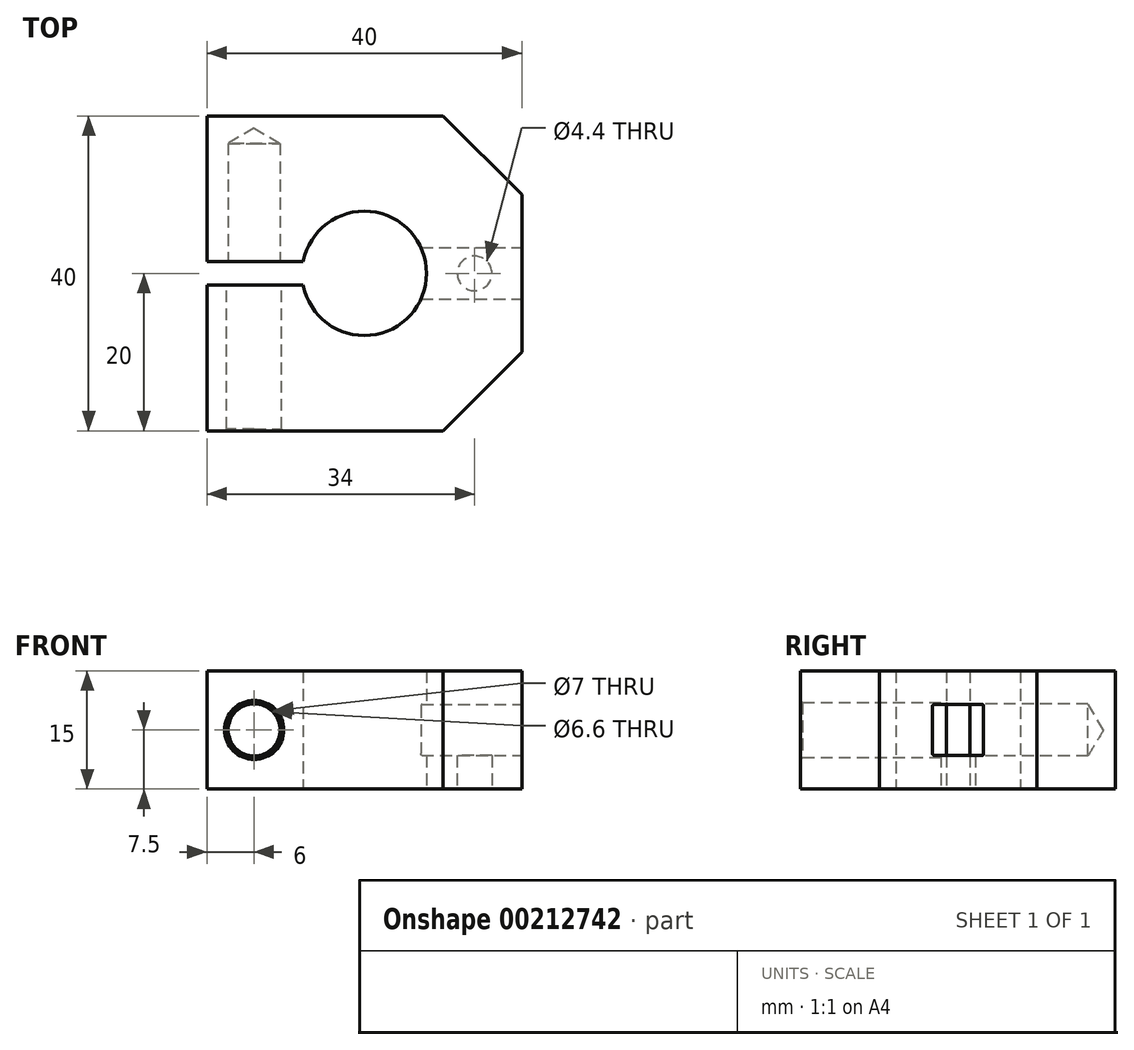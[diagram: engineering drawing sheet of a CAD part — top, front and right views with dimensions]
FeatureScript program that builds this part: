
annotation { "Feature Type Name" : "Feature", "Feature Type Description" : "" }
export const myFeature = defineFeature(function(context is Context, id is Id, definition is map)
    precondition{}
    {
        {
            var Q0;
            Q0=qCreatedBy(makeId("Top.planeOp"),FACE);
            var sketch = newSketch(context, id + "F0", { "sketchPlane" : qUnion([Q0])});
            skLineSegment(sketch, "E0.bottom", {"start": v(20, 20) * mm, "end": v(-20, 20) * mm});
            skLineSegment(sketch, "E0.top", {"start": v(20, -20) * mm, "end": v(-20, -20) * mm});
            skLineSegment(sketch, "E0.left", {"start": v(20, 20) * mm, "end": v(20, -20) * mm});
            skLineSegment(sketch, "E0.right", {"start": v(-20, 20) * mm, "end": v(-20, 1.5) * mm});
            skPoint(sketch, "E0.middle", {"position": v(0, 0) * mm});
            skArc(sketch, "E1", {"start": v(-7.76, -1.5) * mm, "mid": v(7.9, 0) * mm, "end": v(-7.76, 1.5) * mm});
            skLineSegment(sketch, "E2", {"start": v(-20, 0) * mm, "end": v(-7.9, 0) * mm, "construction": true});
            skLineSegment(sketch, "E3.0", {"start": v(-20, -1.5) * mm, "end": v(-7.76, -1.5) * mm});
            skLineSegment(sketch, "E4.0", {"start": v(-20, 1.5) * mm, "end": v(-7.76, 1.5) * mm});
            skLineSegment(sketch, "E5.trimOffspring", {"start": v(-20, -1.5) * mm, "end": v(-20, -20) * mm});
            skSolve(sketch);
        }
        {
            var Q0;
            Q0=makeQuery(id+"F0.imprint","IMPRINT",FACE,{"disambiguationData":[TD([[makeQuery(id+"F0.imprint","IMPRINT",EDGE,{"derivedFrom":sQuery(id+"F0.wireOp",EDGE,"E0.bottom")}),1.0]])]});
            extrude(context, id + "F1", {"entities" : qUnion([Q0]), "depth" : 15 * mm});
        }
        {
            var Q0;
            Q0=qCreatedBy(makeId("Front.planeOp"),FACE);
            var sketch = newSketch(context, id + "F2", { "sketchPlane" : qUnion([Q0])});
            skCircle(sketch, "E6", {"center": v(-14, 7.5) * mm, "radius": 3.5 * mm});
            skSolve(sketch);
        }
        {
            var Q0;
            Q0=makeQuery(id+"F2.imprint","IMPRINT",FACE,{"disambiguationData":[TD([[makeQuery(id+"F2.imprint","IMPRINT",EDGE,{"derivedFrom":sQuery(id+"F2.wireOp",EDGE,"E6")}),1.0]])]});
            extrude(context, id + "F3", {"entities" : qUnion([Q0]), "operationType" : NewBodyOperationType.REMOVE, "depth" : 25 * mm});
        }
        {
            var Q0;
            Q0=makeQuery(id+"F1.opExtrude","SWEPT_FACE",FACE,{"disambiguationData":[OSD([sQuery(id+"F0.wireOp",EDGE,"E4.0")])]});
            var sketch = newSketch(context, id + "F4", { "sketchPlane" : qUnion([Q0])});
            skPoint(sketch, "E7", {"position": v(-14, 7.5) * mm});
            skSolve(sketch);
        }
        {
            var Q0;
            Q0=sQuery(id+"F4.wireOp",VERTEX,"E7");
            var Q1;
            Q1=makeQuery(id+"F1.opExtrude","SWEPT_BODY",BODY,{"disambiguationData":[OSD([sQuery(id+"F0.wireOp",EDGE,"E0.bottom"),sQuery(id+"F0.wireOp",EDGE,"E0.top"),sQuery(id+"F0.wireOp",EDGE,"E0.left"),sQuery(id+"F0.wireOp",EDGE,"E0.right"),sQuery(id+"F0.wireOp",EDGE,"E1"),sQuery(id+"F0.wireOp",EDGE,"E3.0"),sQuery(id+"F0.wireOp",EDGE,"E4.0"),sQuery(id+"F0.wireOp",EDGE,"E5.trimOffspring")])]});
            hole(context, id + "F5", {"style" : HoleStyle.SIMPLE, "endStyle" : HoleEndStyle.BLIND, "standardTappedOrClearance" : lookupTablePath({ "standard" : "ISO", "fit" : "Normal", "size" : "M6", "type" : "Clearance" }), "standardBlindInLast" : lookupTablePath({ "fit" : "Standard", "standard" : "ISO", "size" : "M6", "type" : "Clearance" }), "holeDiameter" : 6.6 * mm, "holeDepth" : 15 * mm, "locations" : qUnion([Q0]), "scope" : qUnion([Q1])});
        }
        {
            var Q0;
            Q0=makeQuery(id+"F1.opExtrude","SWEPT_EDGE",EDGE,{"disambiguationData":[OSD([sQuery(id+"F0.wireOp",EDGE,"E0.top"),sQuery(id+"F0.wireOp",EDGE,"E0.left")])]});
            var Q1;
            Q1=makeQuery(id+"F1.opExtrude","SWEPT_EDGE",EDGE,{"disambiguationData":[OSD([sQuery(id+"F0.wireOp",EDGE,"E0.bottom"),sQuery(id+"F0.wireOp",EDGE,"E0.left")])]});
            chamfer(context, id + "F6", {"entities" : qUnion([Q0, Q1]), "width" : 10 * mm, "tangentPropagation" : true});
        }
        {
            var Q0;
            Q0=makeQuery(id+"F1.opExtrude","SWEPT_FACE",FACE,{"disambiguationData":[OSD([sQuery(id+"F0.wireOp",EDGE,"E0.left")])]});
            var sketch = newSketch(context, id + "F7", { "sketchPlane" : qUnion([Q0])});
            skLineSegment(sketch, "E8.bottom", {"start": v(3.25, 10.75) * mm, "end": v(-3.25, 10.75) * mm});
            skLineSegment(sketch, "E8.top", {"start": v(3.25, 4.25) * mm, "end": v(-3.25, 4.25) * mm});
            skLineSegment(sketch, "E8.left", {"start": v(3.25, 10.75) * mm, "end": v(3.25, 4.25) * mm});
            skLineSegment(sketch, "E8.right", {"start": v(-3.25, 10.75) * mm, "end": v(-3.25, 4.25) * mm});
            skPoint(sketch, "E8.middle", {"position": v(0, 7.5) * mm});
            skSolve(sketch);
        }
        {
            var Q0;
            Q0=makeQuery(id+"F7.imprint","IMPRINT",FACE,{"disambiguationData":[TD([[makeQuery(id+"F7.imprint","IMPRINT",EDGE,{"derivedFrom":sQuery(id+"F7.wireOp",EDGE,"E8.bottom")}),1.0]])]});
            extrude(context, id + "F8", {"entities" : qUnion([Q0]), "operationType" : NewBodyOperationType.REMOVE, "endBound" : BoundingType.UP_TO_NEXT, "oppositeDirection" : true, "depth" : 25 * mm});
        }
        {
            var Q0;
            Q0=makeQuery(id+"F1.opExtrude","CAP_FACE",FACE,{"disambiguationData":[OSD([sQuery(id+"F0.wireOp",EDGE,"E0.bottom"),sQuery(id+"F0.wireOp",EDGE,"E0.top"),sQuery(id+"F0.wireOp",EDGE,"E0.left"),sQuery(id+"F0.wireOp",EDGE,"E0.right"),sQuery(id+"F0.wireOp",EDGE,"E1"),sQuery(id+"F0.wireOp",EDGE,"E3.0"),sQuery(id+"F0.wireOp",EDGE,"E4.0"),sQuery(id+"F0.wireOp",EDGE,"E5.trimOffspring")])],"isStart":true});
            var sketch = newSketch(context, id + "F9", { "sketchPlane" : qUnion([Q0])});
            skPoint(sketch, "E9", {"position": v(14, 0) * mm});
            skSolve(sketch);
        }
        {
            var Q0;
            Q0=sQuery(id+"F9.wireOp",VERTEX,"E9");
            var Q1;
            Q1=makeQuery(id+"F1.opExtrude","SWEPT_BODY",BODY,{"disambiguationData":[OSD([sQuery(id+"F0.wireOp",EDGE,"E0.bottom"),sQuery(id+"F0.wireOp",EDGE,"E0.top"),sQuery(id+"F0.wireOp",EDGE,"E0.left"),sQuery(id+"F0.wireOp",EDGE,"E0.right"),sQuery(id+"F0.wireOp",EDGE,"E1"),sQuery(id+"F0.wireOp",EDGE,"E3.0"),sQuery(id+"F0.wireOp",EDGE,"E4.0"),sQuery(id+"F0.wireOp",EDGE,"E5.trimOffspring")])]});
            hole(context, id + "F10", {"style" : HoleStyle.SIMPLE, "endStyle" : HoleEndStyle.BLIND, "standardTappedOrClearance" : lookupTablePath({ "standard" : "ISO", "fit" : "Normal", "size" : "M4", "type" : "Clearance" }), "standardBlindInLast" : lookupTablePath({ "fit" : "Standard", "standard" : "ISO", "size" : "M4", "type" : "Clearance" }), "holeDiameter" : 4.4 * mm, "holeDepth" : 5 * mm, "locations" : qUnion([Q0]), "scope" : qUnion([Q1])});
        }
        {
            var Q0;
            Q0=makeQuery(id+"F10.hole-0.boolean.opBoolean","COPY",EDGE,{"derivedFrom":makeQuery(id+"F10.hole-0.opRevolve","SWEPT_EDGE",EDGE,{"disambiguationData":[OSD([sQuery(id+"F10.hole-0.sketch.wireOp",EDGE,"core_line_2"),sQuery(id+"F10.hole-0.sketch.wireOp",EDGE,"core_line_3")])]})});
            var Q1;
            Q1=makeQuery(id+"F3.boolean.opBoolean","INTERSECT",EDGE,{"derivedFrom":[makeQuery(id+"F1.opExtrude","SWEPT_FACE",FACE,{"disambiguationData":[OSD([sQuery(id+"F0.wireOp",EDGE,"E0.top")])]}),makeQuery(id+"F3.opExtrude","SWEPT_FACE",FACE,{"disambiguationData":[OSD([sQuery(id+"F2.wireOp",EDGE,"E6")])]})]});
            chamfer(context, id + "F11", {"entities" : qUnion([Q0, Q1]), "width" : 0.25 * mm, "tangentPropagation" : true});
        }
        {
            var Q0;
            Q0=makeQuery(id+"F8.boolean.opBoolean","COPY",EDGE,{"derivedFrom":makeQuery(id+"F8.opExtrude","SWEPT_EDGE",EDGE,{"disambiguationData":[OSD([sQuery(id+"F7.wireOp",EDGE,"E8.top"),sQuery(id+"F7.wireOp",EDGE,"E8.left")])]})});
            var Q1;
            Q1=makeQuery(id+"F8.boolean.opBoolean","COPY",EDGE,{"derivedFrom":makeQuery(id+"F8.opExtrude","SWEPT_EDGE",EDGE,{"disambiguationData":[OSD([sQuery(id+"F7.wireOp",EDGE,"E8.top"),sQuery(id+"F7.wireOp",EDGE,"E8.right")])]})});
            var Q2;
            Q2=makeQuery(id+"F8.boolean.opBoolean","COPY",EDGE,{"derivedFrom":makeQuery(id+"F8.opExtrude","SWEPT_EDGE",EDGE,{"disambiguationData":[OSD([sQuery(id+"F7.wireOp",EDGE,"E8.bottom"),sQuery(id+"F7.wireOp",EDGE,"E8.left")])]})});
            var Q3;
            Q3=makeQuery(id+"F8.boolean.opBoolean","COPY",EDGE,{"derivedFrom":makeQuery(id+"F8.opExtrude","SWEPT_EDGE",EDGE,{"disambiguationData":[OSD([sQuery(id+"F7.wireOp",EDGE,"E8.bottom"),sQuery(id+"F7.wireOp",EDGE,"E8.right")])]})});
            fillet(context, id + "F12", {"entities" : qUnion([Q0, Q1, Q2, Q3]), "radius" : 0.25 * mm, "tangentPropagation" : true, "allowEdgeOverflow" : false});
        }
    });
